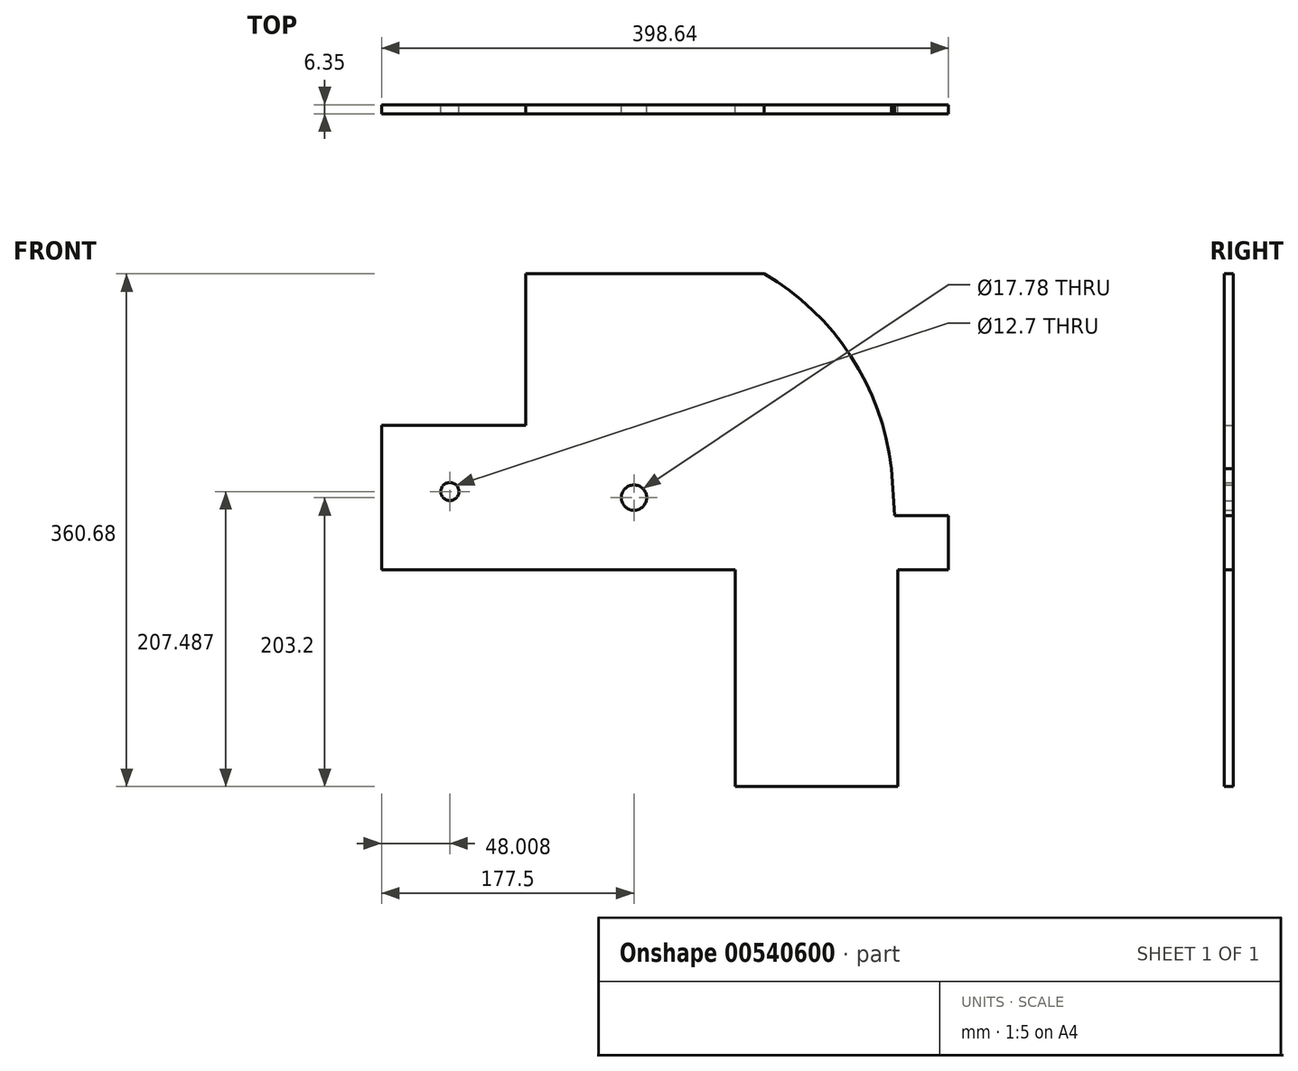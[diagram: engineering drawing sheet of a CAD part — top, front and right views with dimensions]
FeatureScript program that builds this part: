
annotation { "Feature Type Name" : "Feature", "Feature Type Description" : "" }
export const myFeature = defineFeature(function(context is Context, id is Id, definition is map)
    precondition{}
    {
        {
            var Q0;
            Q0=qCreatedBy(makeId("Front.planeOp"),FACE);
            var sketch = newSketch(context, id + "F0", { "sketchPlane" : qUnion([Q0])});
            skCircle(sketch, "E0", {"center": v(0, 50.8) * mm, "radius": 50.8 * mm, "construction": true});
            skArc(sketch, "E1", {"start": v(180.98, 71.12) * mm, "mid": v(152.5, 150.33) * mm, "end": v(91.46, 208.28) * mm});
            skLineSegment(sketch, "E2", {"start": v(180.98, 71.12) * mm, "end": v(185.58, 0) * mm});
            skLineSegment(sketch, "E3", {"start": v(-76.2, 0) * mm, "end": v(-76.2, 208.28) * mm});
            skLineSegment(sketch, "E4", {"start": v(-76.2, 208.28) * mm, "end": v(91.46, 208.28) * mm});
            skCircle(sketch, "E5", {"center": v(0, 50.8) * mm, "radius": 8.9 * mm});
            skLineSegment(sketch, "E6.left", {"start": v(185.58, 0) * mm, "end": v(185.58, -152.4) * mm});
            skLineSegment(sketch, "E7", {"start": v(185.58, -152.4) * mm, "end": v(71.28, -152.4) * mm});
            skLineSegment(sketch, "E8", {"start": v(71.28, -152.4) * mm, "end": v(71.28, 0) * mm});
            skLineSegment(sketch, "E9", {"start": v(71.28, 0) * mm, "end": v(-76.2, 0) * mm});
            skSolve(sketch);
        }
        {
            var Q0;
            Q0 = qSketchRegion(id + "F0", true);
            extrude(context, id + "F1", {"entities" : qUnion([Q0]), "depth" : 6.35 * mm, "offsetDistance" : 25.4 * mm});
        }
        {
            var Q0;
            Q0=qCreatedBy(makeId("Front.planeOp"),FACE);
            var sketch = newSketch(context, id + "F2", { "sketchPlane" : qUnion([Q0])});
            skLineSegment(sketch, "E10.bottom", {"start": v(183.04, 0) * mm, "end": v(221.14, 0) * mm});
            skLineSegment(sketch, "E10.left", {"start": v(185.58, 0) * mm, "end": v(183.1, 38.28) * mm});
            skLineSegment(sketch, "E10.right", {"start": v(221.14, 0) * mm, "end": v(221.14, 38.1) * mm});
            skLineSegment(sketch, "E11", {"start": v(183.1, 38.28) * mm, "end": v(221.14, 38.1) * mm});
            skLineSegment(sketch, "E12", {"start": v(-75.9, 0) * mm, "end": v(-177.5, 0) * mm});
            skLineSegment(sketch, "E13", {"start": v(-177.5, 0) * mm, "end": v(-177.5, 101.6) * mm});
            skLineSegment(sketch, "E14", {"start": v(-177.5, 101.6) * mm, "end": v(-74.75, 101.6) * mm});
            skLineSegment(sketch, "E15", {"start": v(-74.75, 101.6) * mm, "end": v(-75.9, 0) * mm});
            skCircle(sketch, "E16", {"center": v(-129.5, 55.09) * mm, "radius": 6.35 * mm});
            skSolve(sketch);
        }
        {
            var Q0;
            Q0=makeQuery(id+"F2.imprint","IMPRINT",FACE,{"disambiguationData":[TD([[makeQuery(id+"F2.imprint","IMPRINT",EDGE,{"derivedFrom":sQuery(id+"F2.wireOp",EDGE,"E10.bottom")}),1.0]])]});
            var Q1;
            Q1=makeQuery(id+"F2.imprint","IMPRINT",FACE,{"disambiguationData":[TD([[makeQuery(id+"F2.imprint","IMPRINT",EDGE,{"derivedFrom":sQuery(id+"F2.wireOp",EDGE,"E12")}),-1.0]])]});
            extrude(context, id + "F3", {"entities" : qUnion([Q0, Q1]), "operationType" : NewBodyOperationType.ADD, "depth" : 6.35 * mm, "offsetDistance" : 25.4 * mm});
        }
    });
